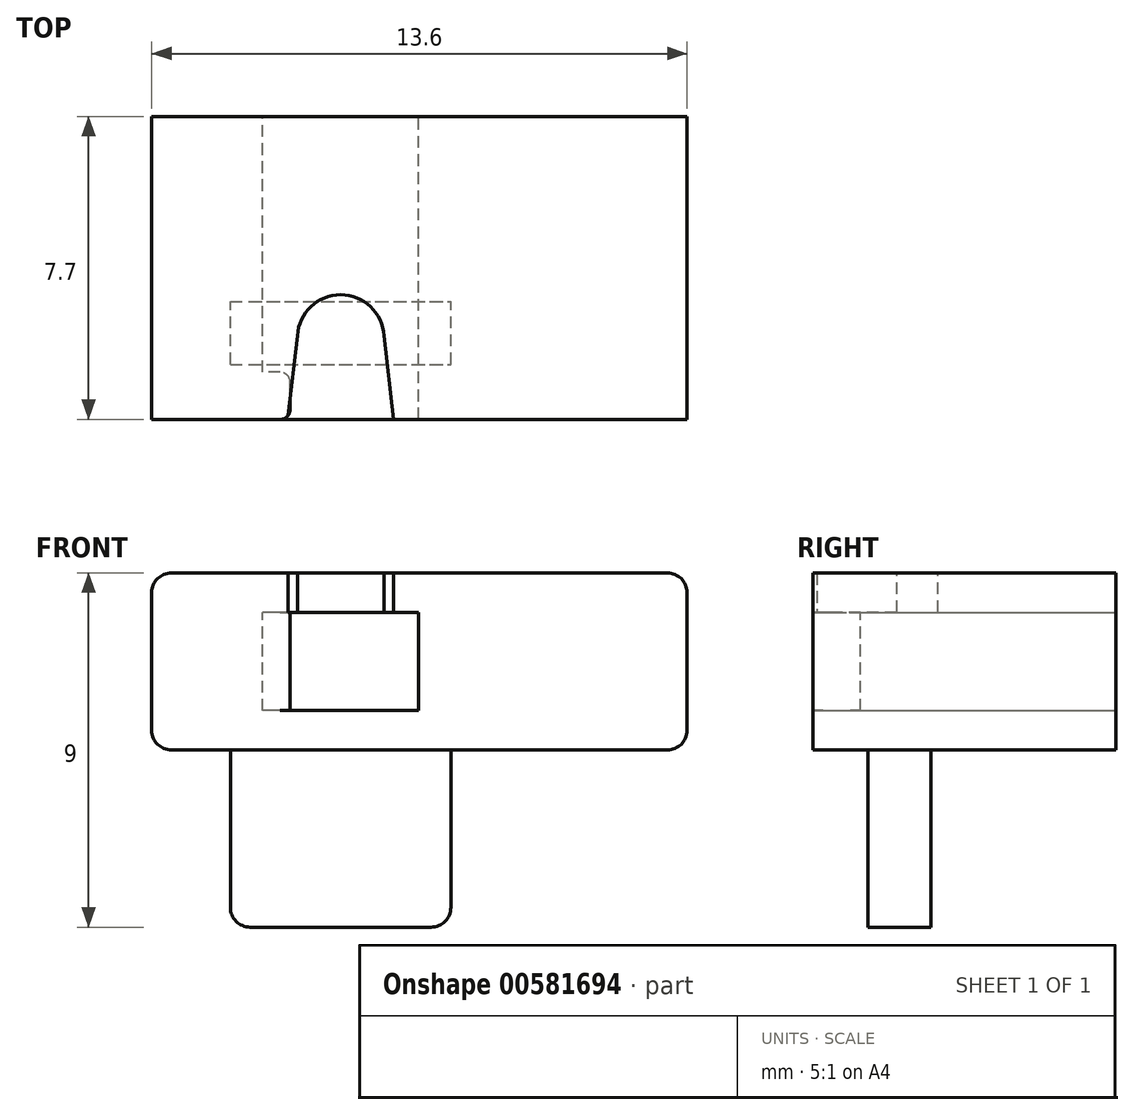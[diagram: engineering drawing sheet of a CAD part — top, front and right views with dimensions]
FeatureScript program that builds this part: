
annotation { "Feature Type Name" : "Feature", "Feature Type Description" : "" }
export const myFeature = defineFeature(function(context is Context, id is Id, definition is map)
    precondition{}
    {
        {
            var Q0;
            Q0=qCreatedBy(makeId("Front.planeOp"),FACE);
            var sketch = newSketch(context, id + "F0", { "sketchPlane" : qUnion([Q0])});
            skLineSegment(sketch, "E0.bottom", {"start": v(2.8, 2.25) * mm, "end": v(-2.8, 2.25) * mm});
            skLineSegment(sketch, "E0.top", {"start": v(2.8, -2.25) * mm, "end": v(-2.8, -2.25) * mm});
            skLineSegment(sketch, "E0.left", {"start": v(2.8, 2.25) * mm, "end": v(2.8, -2.25) * mm});
            skLineSegment(sketch, "E0.right", {"start": v(-2.8, 2.25) * mm, "end": v(-2.8, -2.25) * mm});
            skPoint(sketch, "E0.middle", {"position": v(0, 0) * mm});
            skLineSegment(sketch, "E1.bottom", {"start": v(1.99, 1.25) * mm, "end": v(-1.99, 1.25) * mm});
            skLineSegment(sketch, "E1.top", {"start": v(1.99, -1.25) * mm, "end": v(-1.99, -1.25) * mm});
            skLineSegment(sketch, "E1.left", {"start": v(1.99, 1.25) * mm, "end": v(1.99, -1.25) * mm});
            skLineSegment(sketch, "E1.right", {"start": v(-1.99, 1.25) * mm, "end": v(-1.99, -1.25) * mm});
            skSolve(sketch);
        }
        {
            var Q0;
            Q0=makeQuery(id+"F0.imprint","IMPRINT",FACE,{"disambiguationData":[TD([[makeQuery(id+"F0.imprint","IMPRINT",EDGE,{"derivedFrom":sQuery(id+"F0.wireOp",EDGE,"E0.bottom")}),1.0]])]});
            extrude(context, id + "F1", {"entities" : qUnion([Q0]), "depth" : 7.7 * mm, "offsetDistance" : 25 * mm});
        }
        {
            var Q0;
            Q0=makeQuery(id+"F1.opExtrude","SWEPT_FACE",FACE,{"disambiguationData":[OSD([sQuery(id+"F0.wireOp",EDGE,"E0.top")])]});
            var sketch = newSketch(context, id + "F2", { "sketchPlane" : qUnion([Q0])});
            skLineSegment(sketch, "E2.bottom", {"start": v(-2.8, 6.3) * mm, "end": v(2.8, 6.3) * mm});
            skLineSegment(sketch, "E2.top", {"start": v(-2.8, 4.7) * mm, "end": v(2.8, 4.7) * mm});
            skLineSegment(sketch, "E2.left", {"start": v(-2.8, 6.3) * mm, "end": v(-2.8, 4.7) * mm});
            skLineSegment(sketch, "E2.right", {"start": v(2.8, 6.3) * mm, "end": v(2.8, 4.7) * mm});
            skSolve(sketch);
        }
        {
            var Q0;
            Q0=makeQuery(id+"F2.imprint","IMPRINT",FACE,{"disambiguationData":[TD([[makeQuery(id+"F2.imprint","IMPRINT",EDGE,{"derivedFrom":sQuery(id+"F2.wireOp",EDGE,"E2.bottom")}),-1.0]])]});
            extrude(context, id + "F3", {"entities" : qUnion([Q0]), "operationType" : NewBodyOperationType.ADD, "depth" : 4.5 * mm, "offsetDistance" : 25 * mm});
        }
        {
            var Q0;
            Q0=makeQuery(id+"F1.opExtrude","SWEPT_FACE",FACE,{"disambiguationData":[OSD([sQuery(id+"F0.wireOp",EDGE,"E1.right")])]});
            var sketch = newSketch(context, id + "F4", { "sketchPlane" : qUnion([Q0])});
            skLineSegment(sketch, "E3.bottom", {"start": v(-7.7, -1.25) * mm, "end": v(-6.5, -1.25) * mm});
            skLineSegment(sketch, "E3.top", {"start": v(-7.7, 1.25) * mm, "end": v(-6.5, 1.25) * mm});
            skLineSegment(sketch, "E3.left", {"start": v(-7.7, -1.25) * mm, "end": v(-7.7, 1.25) * mm});
            skLineSegment(sketch, "E3.right", {"start": v(-6.5, -1.25) * mm, "end": v(-6.5, 1.25) * mm});
            skSolve(sketch);
        }
        {
            var Q0;
            Q0=makeQuery(id+"F4.imprint","IMPRINT",FACE,{"disambiguationData":[TD([[makeQuery(id+"F4.imprint","IMPRINT",EDGE,{"derivedFrom":sQuery(id+"F4.wireOp",EDGE,"E3.bottom")}),1.0]])]});
            extrude(context, id + "F5", {"entities" : qUnion([Q0]), "operationType" : NewBodyOperationType.ADD, "depth" : 0.7 * mm, "offsetDistance" : 25 * mm});
        }
        {
            var Q0;
            Q0=makeQuery(id+"F3.boolean.opBoolean","MERGE",FACE,{"derivedFrom":[makeQuery(id+"F1.opExtrude","SWEPT_FACE",FACE,{"disambiguationData":[OSD([sQuery(id+"F0.wireOp",EDGE,"E0.left")])]}),makeQuery(id+"F3.opExtrude","SWEPT_FACE",FACE,{"disambiguationData":[OSD([sQuery(id+"F2.wireOp",EDGE,"E2.right")])]})]});
            var Q1;
            Q1=makeQuery(id+"F3.boolean.opBoolean","MERGE",FACE,{"derivedFrom":[makeQuery(id+"F1.opExtrude","SWEPT_FACE",FACE,{"disambiguationData":[OSD([sQuery(id+"F0.wireOp",EDGE,"E0.right")])]}),makeQuery(id+"F3.opExtrude","SWEPT_FACE",FACE,{"disambiguationData":[OSD([sQuery(id+"F2.wireOp",EDGE,"E2.left")])]})]});
            cPlane(context, id + "F6", {"entities" : qUnion([Q0, Q1]), "cplaneType" : CPlaneType.MID_PLANE, "offset" : 25 * mm, "width" : 150 * mm, "height" : 150 * mm});
        }
        {
            var Q0;
            Q0=makeQuery(id+"F3.boolean.opBoolean","MERGE",FACE,{"derivedFrom":[makeQuery(id+"F1.opExtrude","SWEPT_FACE",FACE,{"disambiguationData":[OSD([sQuery(id+"F0.wireOp",EDGE,"E0.left")])]}),makeQuery(id+"F3.opExtrude","SWEPT_FACE",FACE,{"disambiguationData":[OSD([sQuery(id+"F2.wireOp",EDGE,"E2.right")])]})]});
            var sketch = newSketch(context, id + "F7", { "sketchPlane" : qUnion([Q0])});
            skLineSegment(sketch, "E4.bottom", {"start": v(-7.7, 2.25) * mm, "end": v(0, 2.25) * mm});
            skLineSegment(sketch, "E4.top", {"start": v(-7.7, -2.25) * mm, "end": v(0, -2.25) * mm});
            skLineSegment(sketch, "E4.left", {"start": v(-7.7, 2.25) * mm, "end": v(-7.7, -2.25) * mm});
            skLineSegment(sketch, "E4.right", {"start": v(0, 2.25) * mm, "end": v(0, -2.25) * mm});
            skSolve(sketch);
        }
        {
            var Q0;
            Q0=makeQuery(id+"F7.imprint","IMPRINT",FACE,{"disambiguationData":[TD([[makeQuery(id+"F7.imprint","IMPRINT",EDGE,{"derivedFrom":sQuery(id+"F7.wireOp",EDGE,"E4.bottom")}),-1.0]])]});
            extrude(context, id + "F8", {"entities" : qUnion([Q0]), "operationType" : NewBodyOperationType.ADD, "depth" : 6 * mm, "offsetDistance" : 25 * mm});
        }
        {
            var Q0;
            Q0=makeQuery(id+"F8.boolean.opBoolean","MERGE",FACE,{"derivedFrom":[makeQuery(id+"F1.opExtrude","SWEPT_FACE",FACE,{"disambiguationData":[OSD([sQuery(id+"F0.wireOp",EDGE,"E0.bottom")])]}),makeQuery(id+"F8.opExtrude","SWEPT_FACE",FACE,{"disambiguationData":[OSD([sQuery(id+"F7.wireOp",EDGE,"E4.bottom")])]})]});
            var sketch = newSketch(context, id + "F9", { "sketchPlane" : qUnion([Q0])});
            skCircle(sketch, "E5", {"center": v(0, -5.63) * mm, "radius": 1.1 * mm});
            skLineSegment(sketch, "E6", {"start": v(1.1, -5.57) * mm, "end": v(1.35, -7.7) * mm});
            skLineSegment(sketch, "E7", {"start": v(-1.1, -5.57) * mm, "end": v(-1.35, -7.7) * mm});
            skLineSegment(sketch, "E8", {"start": v(0, -5.63) * mm, "end": v(0, -3.09) * mm});
            skLineSegment(sketch, "E9", {"start": v(-1.35, -7.7) * mm, "end": v(1.35, -7.7) * mm});
            skSolve(sketch);
        }
        {
            var Q0;
            {var subQ0=sQuery(id+"F9.wireOp",EDGE,"E5");var subQ2=makeQuery(id+"F9.imprint","IMPRINT",VERTEX,{"derivedFrom":subQ0});Q0=makeQuery(id+"F9.imprint","IMPRINT",FACE,{"disambiguationData":[TD([[makeQuery(id+"F9.imprint","IMPRINT",EDGE,{"disambiguationData":[TD([[subQ2,1.0]])],"derivedFrom":subQ0}),1.0]])]});}
            var Q1;
            {var subQ0=sQuery(id+"F9.wireOp",EDGE,"E6");Q1=makeQuery(id+"F9.imprint","IMPRINT",FACE,{"disambiguationData":[TD([[makeQuery(id+"F9.imprint","IMPRINT",EDGE,{"derivedFrom":subQ0}),-1.0]])]});}
            extrude(context, id + "F10", {"entities" : qUnion([Q0, Q1]), "operationType" : NewBodyOperationType.REMOVE, "oppositeDirection" : true, "depth" : 1 * mm, "offsetDistance" : 25 * mm});
        }
        {
            var Q0;
            Q0=makeQuery(id+"F3.boolean.opBoolean","MERGE",FACE,{"derivedFrom":[makeQuery(id+"F1.opExtrude","SWEPT_FACE",FACE,{"disambiguationData":[OSD([sQuery(id+"F0.wireOp",EDGE,"E0.right")])]}),makeQuery(id+"F3.opExtrude","SWEPT_FACE",FACE,{"disambiguationData":[OSD([sQuery(id+"F2.wireOp",EDGE,"E2.left")])]})]});
            var sketch = newSketch(context, id + "F11", { "sketchPlane" : qUnion([Q0])});
            skLineSegment(sketch, "E10.bottom", {"start": v(7.7, 2.25) * mm, "end": v(0, 2.25) * mm});
            skLineSegment(sketch, "E10.top", {"start": v(7.7, -2.25) * mm, "end": v(0, -2.25) * mm});
            skLineSegment(sketch, "E10.left", {"start": v(7.7, 2.25) * mm, "end": v(7.7, -2.25) * mm});
            skLineSegment(sketch, "E10.right", {"start": v(0, 2.25) * mm, "end": v(0, -2.25) * mm});
            skSolve(sketch);
        }
        {
            var Q0;
            Q0=makeQuery(id+"F11.imprint","IMPRINT",FACE,{"disambiguationData":[TD([[makeQuery(id+"F11.imprint","IMPRINT",EDGE,{"derivedFrom":sQuery(id+"F11.wireOp",EDGE,"E10.bottom")}),1.0]])]});
            extrude(context, id + "F12", {"entities" : qUnion([Q0]), "operationType" : NewBodyOperationType.ADD, "depth" : 2 * mm, "offsetDistance" : 25 * mm});
        }
        {
            var Q0;
            Q0=makeQuery(id+"F8.opExtrude","CAP_EDGE",EDGE,{"disambiguationData":[OSD([sQuery(id+"F7.wireOp",EDGE,"E4.top")])],"isStart":false});
            var Q1;
            Q1=makeQuery(id+"F8.opExtrude","CAP_EDGE",EDGE,{"disambiguationData":[OSD([sQuery(id+"F7.wireOp",EDGE,"E4.bottom")])],"isStart":false});
            var Q2;
            Q2=makeQuery(id+"F3.opExtrude","CAP_EDGE",EDGE,{"disambiguationData":[OSD([sQuery(id+"F2.wireOp",EDGE,"E2.right")])],"isStart":false});
            var Q3;
            Q3=makeQuery(id+"F12.opExtrude","CAP_EDGE",EDGE,{"disambiguationData":[OSD([sQuery(id+"F11.wireOp",EDGE,"E10.bottom")])],"isStart":false});
            var Q4;
            Q4=makeQuery(id+"F12.opExtrude","CAP_EDGE",EDGE,{"disambiguationData":[OSD([sQuery(id+"F11.wireOp",EDGE,"E10.top")])],"isStart":false});
            var Q5;
            Q5=makeQuery(id+"F3.opExtrude","CAP_EDGE",EDGE,{"disambiguationData":[OSD([sQuery(id+"F2.wireOp",EDGE,"E2.left")])],"isStart":false});
            fillet(context, id + "F13", {"entities" : qUnion([Q0, Q1, Q2, Q3, Q4, Q5]), "radius" : 0.5 * mm, "tangentPropagation" : true, "allowEdgeOverflow" : false});
        }
        {
            var Q0;
            Q0=makeQuery(id+"F5.opExtrude","CAP_EDGE",EDGE,{"disambiguationData":[OSD([sQuery(id+"F4.wireOp",EDGE,"E3.left")])],"isStart":false});
            var Q1;
            Q1=makeQuery(id+"F5.opExtrude","CAP_EDGE",EDGE,{"disambiguationData":[OSD([sQuery(id+"F4.wireOp",EDGE,"E3.right")])],"isStart":false});
            var Q2;
            Q2=makeQuery(id+"Fwh2Z4fw0V1u2xd_1.1.F5.opExtrude","CAP_EDGE",EDGE,{"disambiguationData":[OSD([sQuery(id+"F4.wireOp",EDGE,"E3.left")])],"isStart":false});
            var Q3;
            Q3=makeQuery(id+"Fwh2Z4fw0V1u2xd_1.1.F5.opExtrude","CAP_EDGE",EDGE,{"disambiguationData":[OSD([sQuery(id+"F4.wireOp",EDGE,"E3.right")])],"isStart":false});
            fillet(context, id + "F14", {"entities" : qUnion([Q0, Q1, Q2, Q3]), "radius" : 0.25 * mm, "tangentPropagation" : true, "allowEdgeOverflow" : false});
        }
    });
